# Revit family: PRE070002-FR
name_source: partatom
category: Appareils sanitaires
revit_build: Autodesk Revit 2017 (Build: 20160225_1515(x64)
units: mm (PartAtom-declared; Revit-internal decimal feet)

## family parameters
Basée sur le plan de construction = Non
Cote de connecteur circulaire = Utiliser le diamètre
Couper avec des vides une fois chargée = Non
Partagée = Non
Point de calcul de pièce = Non
Toujours verticalement = Oui
Type d'élément = Normal

## types (4) — shared parameters
Adresse = 7, RUE RACINE - 92542 MONTROUGE CEDEX FRANCE
Debit = 0,30 l/s at 3 bar
Diamètre = 15 mm  [stored 0.0492126 ft]
Fabricant = LES ROBINETS PRESTO S.A.
Finition = Plaque de commande en inox brossée 304L anitvandalisme
Flux = 0.2 L/s
Fonction = Delivered product with 0,15l / s flow regulator (for ordinary urinals)
Delivered with 1 mounting box, 1 stopvalve, dowels and fixing screws.
Garantie = 3
Hauteur = 135 mm  [stored 0.442913 ft]
Largeur = 153 mm  [stored 0.501969 ft]
Lien CCTP = http://www.prestodatashare.com
Lien fiche produit = http://www.prestodatashare.com
Lien notice d'utilisation = http://www.prestodatashare.com
Matériau = Laiton poli chromé
Perte de charge = 0.0 Pa
Pression = 1 à 5 bars
Profondeur = 58 mm
Raccordement = M G 1/2" Inlet and outlet
URL = http://www.prestodatashare.com
URL Fabricant = http://www.prestodatashare.com
Variantes = 55444-55442-55438-55440

## per-type parameters (varying)
| type | Description | Polantis code | Reference |
| 55444 - PRESTO SENSAO 8100N encastré, alimentation secteur | Electronic urinal faucet for flush mounting with automatic optoelectronic detection, anti-vandalism system and closing safety in case of mains failure, mains power supply (transformer not supplied). | PRE070002 | 55444 |
| 55440 - PRESTO SENSAO 8600N ENCASTRE ANTIVANDALISME - Alimentation secteur | Electronic urinal faucet for flush mounting with automatic optoelectronic detection with possibility of forced flushing with manual button, vandal-proof system and closing safety in case of mains failure. or degradation of the detector, 230 V AC transformer power supply (not supplied). | PRE070002c | 55440 |
| 55438 - PRESTO SENSAO 8500N ENCASTRE ANTIVANDALISME - Alimentation pile | Electronic urinal valve for flush mounting with automatic optoelectronic detection with possibility of forced flushing with manual button, vandal-proof system and closing safety in case of battery wear, electric power supply via 6V CRP2 lithium battery. | PRE070002b | 55438 |
| 55442 - PRESTO SENSAO 8300N encastré, alimentation pile | Electronic tap for urinal for flush mounting with automatic optoelectronic detection, anti-vandalism system and closing safety in case of battery wear, power supply by 6V CRP2 type lithium battery. | PRE070002a | 55442 |

note: column(s) folded — value = type name in every type: Modèle

note: [stored X ft] marks values corroborated as IEEE doubles in the binary element streams (Revit-internal decimal feet)
